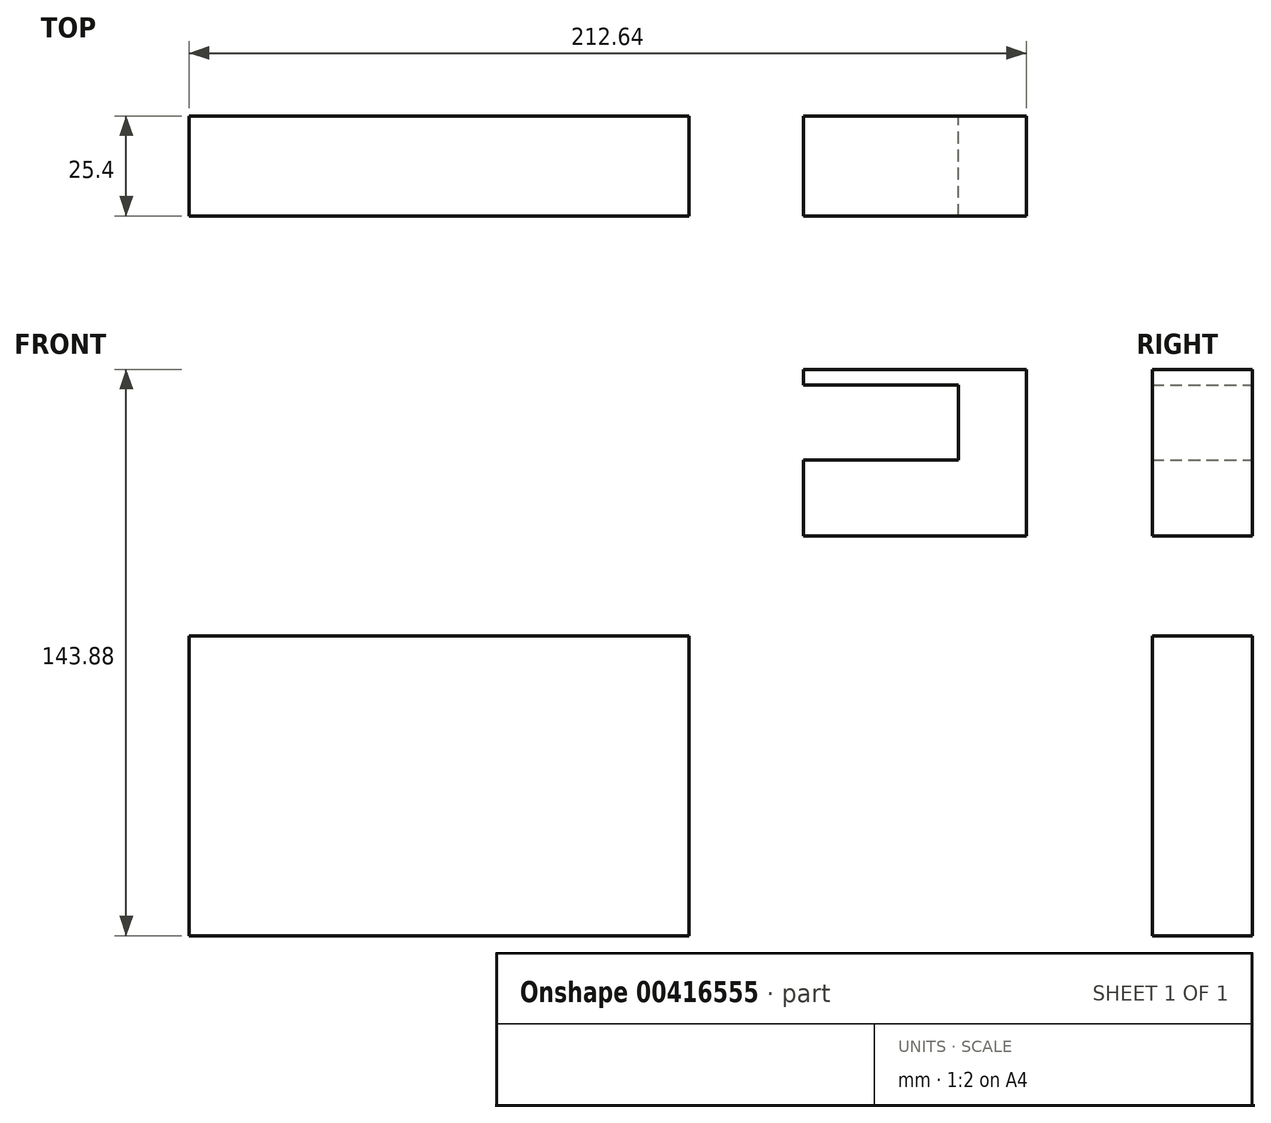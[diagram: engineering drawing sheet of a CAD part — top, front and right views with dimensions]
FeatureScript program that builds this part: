
annotation { "Feature Type Name" : "Feature", "Feature Type Description" : "" }
export const myFeature = defineFeature(function(context is Context, id is Id, definition is map)
    precondition{}
    {
        {
            var Q0;
            Q0=qCreatedBy(makeId("Front.planeOp"),FACE);
            var sketch = newSketch(context, id + "F0", { "sketchPlane" : qUnion([Q0])});
            skLineSegment(sketch, "E0.bottom", {"start": v(63.5, 38.1) * mm, "end": v(-63.5, 38.1) * mm});
            skLineSegment(sketch, "E0.top", {"start": v(63.5, -38.1) * mm, "end": v(-63.5, -38.1) * mm});
            skLineSegment(sketch, "E0.left", {"start": v(63.5, 38.1) * mm, "end": v(63.5, -38.1) * mm});
            skLineSegment(sketch, "E0.right", {"start": v(-63.5, 38.1) * mm, "end": v(-63.5, -38.1) * mm});
            skPoint(sketch, "E0.middle", {"position": v(0, 0) * mm});
            skLineSegment(sketch, "E1.bottom", {"start": v(149.14, 63.5) * mm, "end": v(92.54, 63.5) * mm});
            skLineSegment(sketch, "E1.top", {"start": v(149.14, 105.78) * mm, "end": v(92.54, 105.78) * mm});
            skLineSegment(sketch, "E1.left", {"start": v(149.14, 63.5) * mm, "end": v(149.14, 105.78) * mm});
            skLineSegment(sketch, "E1.right", {"start": v(92.54, 63.5) * mm, "end": v(92.54, 105.78) * mm});
            skPoint(sketch, "E1.middle", {"position": v(120.84, 84.64) * mm});
            skLineSegment(sketch, "E2", {"start": v(29.49, 38.1) * mm, "end": v(29.49, 57.31) * mm});
            skArc(sketch, "E3", {"start": v(54.89, 82.71) * mm, "mid": v(36.93, 75.28) * mm, "end": v(29.49, 57.31) * mm});
            skLineSegment(sketch, "E4", {"start": v(54.89, 82.71) * mm, "end": v(131.93, 82.71) * mm});
            skLineSegment(sketch, "E5.0", {"start": v(54.89, 101.76) * mm, "end": v(131.93, 101.76) * mm});
            skArc(sketch, "E5.1", {"start": v(54.89, 101.76) * mm, "mid": v(23.46, 88.75) * mm, "end": v(10.44, 57.31) * mm});
            skLineSegment(sketch, "E5.2", {"start": v(10.44, 38.1) * mm, "end": v(10.44, 57.31) * mm});
            skLineSegment(sketch, "E6", {"start": v(131.93, 82.71) * mm, "end": v(131.93, 101.76) * mm});
            skFitSpline(sketch, "E7", {"points": [v(-63.5, 38.1) * mm, v(-29.24, 121.37) * mm, v(72.14, 101.76) * mm], "startDerivative": vector(-193.85, 216.52) * mm, "endDerivative": vector(148.82, -117.38) * mm});
            skSolve(sketch);
        }
        {
            var Q0;
            Q0=makeQuery(id+"F0.imprint","IMPRINT",FACE,{"disambiguationData":[TD([[makeQuery(id+"F0.imprint","IMPRINT",EDGE,{"derivedFrom":sQuery(id+"F0.wireOp",EDGE,"E0.top")}),-1.0]])]});
            var Q1;
            {var subQ1=sQuery(id+"F0.wireOp",EDGE,"E1.bottom");Q1=makeQuery(id+"F0.imprint","IMPRINT",FACE,{"disambiguationData":[TD([[makeQuery(id+"F0.imprint","IMPRINT",EDGE,{"derivedFrom":subQ1}),-1.0]])]});}
            extrude(context, id + "F1", {"entities" : qUnion([Q0, Q1]), "endBound" : BoundingType.SYMMETRIC, "depth" : 25.4 * mm});
        }
    });
